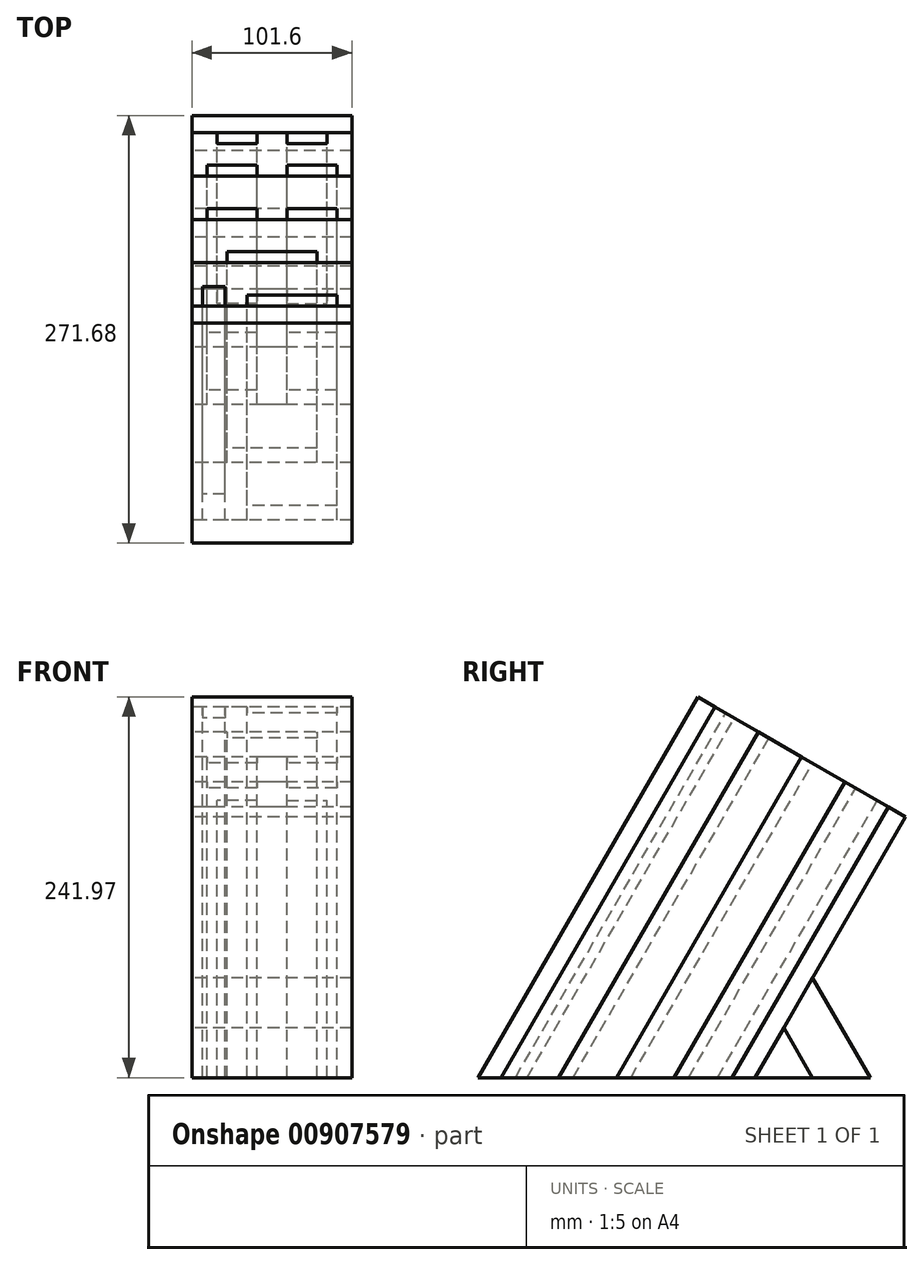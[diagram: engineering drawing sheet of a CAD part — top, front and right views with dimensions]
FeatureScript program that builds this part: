
annotation { "Feature Type Name" : "Feature", "Feature Type Description" : "" }
export const myFeature = defineFeature(function(context is Context, id is Id, definition is map)
    precondition{}
    {
        {
            var Q0;
            Q0=qCreatedBy(makeId("Right.planeOp"),FACE);
            var sketch = newSketch(context, id + "F0", { "sketchPlane" : qUnion([Q0])});
            skLineSegment(sketch, "E0", {"start": v(0, 0) * mm, "end": v(139.7, 241.97) * mm});
            skLineSegment(sketch, "E1", {"start": v(0, 0) * mm, "end": v(175.98, 0) * mm});
            skLineSegment(sketch, "E2", {"start": v(175.98, 0) * mm, "end": v(271.68, 165.77) * mm});
            skLineSegment(sketch, "E3", {"start": v(139.7, 241.97) * mm, "end": v(271.68, 165.77) * mm});
            skLineSegment(sketch, "E4", {"start": v(212.64, 63.5) * mm, "end": v(249.3, 0) * mm});
            skLineSegment(sketch, "E5", {"start": v(249.3, 0) * mm, "end": v(175.98, 0) * mm});
            skLineSegment(sketch, "E6", {"start": v(150.7, 235.62) * mm, "end": v(14.66, 0) * mm});
            skLineSegment(sketch, "E7", {"start": v(178.2, 219.74) * mm, "end": v(51.33, 0) * mm});
            skLineSegment(sketch, "E8", {"start": v(205.7, 203.87) * mm, "end": v(87.99, 0) * mm});
            skLineSegment(sketch, "E9", {"start": v(233.19, 188) * mm, "end": v(124.65, 0) * mm});
            skLineSegment(sketch, "E10", {"start": v(260.68, 172.12) * mm, "end": v(161.31, 0) * mm});
            skLineSegment(sketch, "E11", {"start": v(212.64, 0) * mm, "end": v(194.3, 31.75) * mm});
            skSolve(sketch);
        }
        {
            var Q0;
            {var subQ0=sQuery(id+"F0.wireOp",EDGE,"E0");Q0=makeQuery(id+"F0.imprint","IMPRINT",FACE,{"disambiguationData":[TD([[makeQuery(id+"F0.imprint","IMPRINT",EDGE,{"derivedFrom":subQ0}),-1.0]])]});}
            extrude(context, id + "F1", {"entities" : qUnion([Q0]), "depth" : 101.6 * mm, "offsetDistance" : 25.4 * mm});
        }
        {
            var Q0;
            {var subQ0=sQuery(id+"F0.wireOp",EDGE,"E6");Q0=makeQuery(id+"F0.imprint","IMPRINT",FACE,{"disambiguationData":[TD([[makeQuery(id+"F0.imprint","IMPRINT",EDGE,{"derivedFrom":subQ0}),1.0]])]});}
            extrude(context, id + "F2", {"entities" : qUnion([Q0]), "depth" : 101.6 * mm, "offsetDistance" : 25.4 * mm});
        }
        {
            var Q0;
            {var subQ0=sQuery(id+"F0.wireOp",EDGE,"E7");Q0=makeQuery(id+"F0.imprint","IMPRINT",FACE,{"disambiguationData":[TD([[makeQuery(id+"F0.imprint","IMPRINT",EDGE,{"derivedFrom":subQ0}),1.0]])]});}
            extrude(context, id + "F3", {"entities" : qUnion([Q0]), "depth" : 101.6 * mm, "offsetDistance" : 25.4 * mm});
        }
        {
            var Q0;
            {var subQ0=sQuery(id+"F0.wireOp",EDGE,"E8");Q0=makeQuery(id+"F0.imprint","IMPRINT",FACE,{"disambiguationData":[TD([[makeQuery(id+"F0.imprint","IMPRINT",EDGE,{"derivedFrom":subQ0}),1.0]])]});}
            extrude(context, id + "F4", {"entities" : qUnion([Q0]), "depth" : 101.6 * mm, "offsetDistance" : 25.4 * mm});
        }
        {
            var Q0;
            {var subQ0=sQuery(id+"F0.wireOp",EDGE,"E9");Q0=makeQuery(id+"F0.imprint","IMPRINT",FACE,{"disambiguationData":[TD([[makeQuery(id+"F0.imprint","IMPRINT",EDGE,{"derivedFrom":subQ0}),1.0]])]});}
            extrude(context, id + "F5", {"entities" : qUnion([Q0]), "depth" : 101.6 * mm, "offsetDistance" : 25.4 * mm});
        }
        {
            var Q0;
            {var subQ3=sQuery(id+"F0.wireOp",EDGE,"E10");Q0=makeQuery(id+"F0.imprint","IMPRINT",FACE,{"disambiguationData":[TD([[makeQuery(id+"F0.imprint","IMPRINT",EDGE,{"derivedFrom":subQ3}),1.0]])]});}
            extrude(context, id + "F6", {"entities" : qUnion([Q0]), "depth" : 101.6 * mm, "offsetDistance" : 25.4 * mm});
        }
        {
            var Q0;
            {var subQ3=sQuery(id+"F0.wireOp",EDGE,"E11");Q0=makeQuery(id+"F0.imprint","IMPRINT",FACE,{"disambiguationData":[TD([[makeQuery(id+"F0.imprint","IMPRINT",EDGE,{"derivedFrom":subQ3}),1.0]])]});}
            extrude(context, id + "F7", {"entities" : qUnion([Q0]), "depth" : 101.6 * mm, "offsetDistance" : 25.4 * mm});
        }
        {
            var Q0;
            {var subQ0=sQuery(id+"F0.wireOp",EDGE,"E4");Q0=makeQuery(id+"F0.imprint","IMPRINT",FACE,{"disambiguationData":[TD([[makeQuery(id+"F0.imprint","IMPRINT",EDGE,{"derivedFrom":subQ0}),-1.0]])]});}
            extrude(context, id + "F8", {"entities" : qUnion([Q0]), "depth" : 101.6 * mm, "offsetDistance" : 25.4 * mm});
        }
        {
            var Q0;
            Q0=makeQuery(id+"F2.opExtrude","SWEPT_FACE",FACE,{"disambiguationData":[OSD([sQuery(id+"F0.wireOp",EDGE,"E3")])]});
            var sketch = newSketch(context, id + "F9", { "sketchPlane" : qUnion([Q0])});
            skLineSegment(sketch, "E12.bottom", {"start": v(92.08, 12.7) * mm, "end": v(34.92, 12.7) * mm});
            skLineSegment(sketch, "E12.top", {"start": v(92.08, 20.64) * mm, "end": v(34.92, 20.64) * mm});
            skLineSegment(sketch, "E12.left", {"start": v(92.08, 12.7) * mm, "end": v(92.08, 20.64) * mm});
            skLineSegment(sketch, "E12.right", {"start": v(34.92, 12.7) * mm, "end": v(34.92, 20.64) * mm});
            skLineSegment(sketch, "E13.bottom", {"start": v(21.04, 12.7) * mm, "end": v(6.76, 12.7) * mm});
            skLineSegment(sketch, "E13.top", {"start": v(21.04, 26.99) * mm, "end": v(6.76, 26.99) * mm});
            skLineSegment(sketch, "E13.left", {"start": v(21.04, 12.7) * mm, "end": v(21.04, 26.99) * mm});
            skLineSegment(sketch, "E13.right", {"start": v(6.76, 12.7) * mm, "end": v(6.76, 26.99) * mm});
            skLineSegment(sketch, "E14.bottom", {"start": v(79.38, 44.45) * mm, "end": v(22.22, 44.45) * mm});
            skLineSegment(sketch, "E14.top", {"start": v(79.38, 52.4) * mm, "end": v(22.22, 52.4) * mm});
            skLineSegment(sketch, "E14.left", {"start": v(79.38, 44.45) * mm, "end": v(79.38, 52.4) * mm});
            skLineSegment(sketch, "E14.right", {"start": v(22.22, 44.45) * mm, "end": v(22.22, 52.4) * mm});
            skLineSegment(sketch, "E15.bottom", {"start": v(92.08, 76.2) * mm, "end": v(60.33, 76.2) * mm});
            skLineSegment(sketch, "E15.top", {"start": v(92.08, 84.15) * mm, "end": v(60.33, 84.15) * mm});
            skLineSegment(sketch, "E15.left", {"start": v(92.08, 76.2) * mm, "end": v(92.08, 84.15) * mm});
            skLineSegment(sketch, "E15.right", {"start": v(60.33, 76.2) * mm, "end": v(60.33, 84.15) * mm});
            skLineSegment(sketch, "E16.bottom", {"start": v(41.28, 76.2) * mm, "end": v(9.53, 76.2) * mm});
            skLineSegment(sketch, "E16.top", {"start": v(41.28, 84.15) * mm, "end": v(9.53, 84.15) * mm});
            skLineSegment(sketch, "E16.left", {"start": v(41.28, 76.2) * mm, "end": v(41.28, 84.15) * mm});
            skLineSegment(sketch, "E16.right", {"start": v(9.53, 76.2) * mm, "end": v(9.53, 84.15) * mm});
            skLineSegment(sketch, "E17", {"start": v(50.8, 12.7) * mm, "end": v(50.8, 130.02) * mm, "construction": true});
            skLineSegment(sketch, "E18.bottom", {"start": v(92.07, 107.95) * mm, "end": v(60.33, 107.95) * mm});
            skLineSegment(sketch, "E18.top", {"start": v(92.07, 115.9) * mm, "end": v(60.33, 115.9) * mm});
            skLineSegment(sketch, "E18.left", {"start": v(92.08, 107.95) * mm, "end": v(92.08, 115.9) * mm});
            skLineSegment(sketch, "E18.right", {"start": v(60.33, 107.95) * mm, "end": v(60.33, 115.9) * mm});
            skLineSegment(sketch, "E19.bottom", {"start": v(41.28, 107.95) * mm, "end": v(9.53, 107.95) * mm});
            skLineSegment(sketch, "E19.top", {"start": v(41.28, 115.9) * mm, "end": v(9.53, 115.9) * mm});
            skLineSegment(sketch, "E19.left", {"start": v(41.28, 107.95) * mm, "end": v(41.28, 115.9) * mm});
            skLineSegment(sketch, "E19.right", {"start": v(9.53, 107.95) * mm, "end": v(9.53, 115.9) * mm});
            skLineSegment(sketch, "E20.bottom", {"start": v(60.33, 139.7) * mm, "end": v(85.73, 139.7) * mm});
            skLineSegment(sketch, "E20.top", {"start": v(60.33, 131.75) * mm, "end": v(85.73, 131.75) * mm});
            skLineSegment(sketch, "E20.left", {"start": v(60.33, 139.7) * mm, "end": v(60.33, 131.75) * mm});
            skLineSegment(sketch, "E20.right", {"start": v(85.73, 139.7) * mm, "end": v(85.73, 131.75) * mm});
            skLineSegment(sketch, "E21.MirrorCS", {"start": v(41.28, 139.7) * mm, "end": v(41.28, 131.75) * mm});
            skLineSegment(sketch, "E22.MirrorCS", {"start": v(41.28, 139.7) * mm, "end": v(15.88, 139.7) * mm});
            skLineSegment(sketch, "E23.MirrorCS", {"start": v(15.88, 139.7) * mm, "end": v(15.88, 131.75) * mm});
            skLineSegment(sketch, "E24.MirrorCS", {"start": v(41.28, 131.75) * mm, "end": v(15.88, 131.75) * mm});
            skSolve(sketch);
        }
        {
            var Q0;
            Q0=makeQuery(id+"F9.imprint","IMPRINT",FACE,{"disambiguationData":[TD([[makeQuery(id+"F9.imprint","IMPRINT",EDGE,{"derivedFrom":sQuery(id+"F9.wireOp",EDGE,"E12.bottom")}),-1.0]])]});
            var Q1;
            Q1=makeQuery(id+"F9.imprint","IMPRINT",FACE,{"disambiguationData":[TD([[makeQuery(id+"F9.imprint","IMPRINT",EDGE,{"derivedFrom":sQuery(id+"F9.wireOp",EDGE,"E13.bottom")}),-1.0]])]});
            var Q2;
            Q2=makeQuery(id+"F9.imprint","IMPRINT",FACE,{"disambiguationData":[TD([[makeQuery(id+"F9.imprint","IMPRINT",EDGE,{"derivedFrom":sQuery(id+"F9.wireOp",EDGE,"E14.bottom")}),-1.0]])]});
            var Q3;
            Q3=makeQuery(id+"F9.imprint","IMPRINT",FACE,{"disambiguationData":[TD([[makeQuery(id+"F9.imprint","IMPRINT",EDGE,{"derivedFrom":sQuery(id+"F9.wireOp",EDGE,"E18.bottom")}),-1.0]])]});
            var Q4;
            Q4=makeQuery(id+"F9.imprint","IMPRINT",FACE,{"disambiguationData":[TD([[makeQuery(id+"F9.imprint","IMPRINT",EDGE,{"derivedFrom":sQuery(id+"F9.wireOp",EDGE,"E19.bottom")}),-1.0]])]});
            var Q5;
            Q5=makeQuery(id+"F9.imprint","IMPRINT",FACE,{"disambiguationData":[TD([[makeQuery(id+"F9.imprint","IMPRINT",EDGE,{"derivedFrom":sQuery(id+"F9.wireOp",EDGE,"E20.bottom")}),-1.0]])]});
            var Q6;
            Q6=makeQuery(id+"F9.imprint","IMPRINT",FACE,{"disambiguationData":[TD([[makeQuery(id+"F9.imprint","IMPRINT",EDGE,{"derivedFrom":sQuery(id+"F9.wireOp",EDGE,"E21.MirrorCS")}),-1.0]])]});
            var Q7;
            Q7=makeQuery(id+"F9.imprint","IMPRINT",FACE,{"disambiguationData":[TD([[makeQuery(id+"F9.imprint","IMPRINT",EDGE,{"derivedFrom":sQuery(id+"F9.wireOp",EDGE,"E15.bottom")}),-1.0]])]});
            var Q8;
            Q8=makeQuery(id+"F9.imprint","IMPRINT",FACE,{"disambiguationData":[TD([[makeQuery(id+"F9.imprint","IMPRINT",EDGE,{"derivedFrom":sQuery(id+"F9.wireOp",EDGE,"E16.bottom")}),-1.0]])]});
            extrude(context, id + "F10", {"entities" : qUnion([Q0, Q1, Q2, Q3, Q4, Q5, Q6, Q7, Q8]), "operationType" : NewBodyOperationType.REMOVE, "endBound" : BoundingType.THROUGH_ALL, "oppositeDirection" : true, "depth" : 25.4 * mm, "offsetDistance" : 25.4 * mm});
        }
    });
